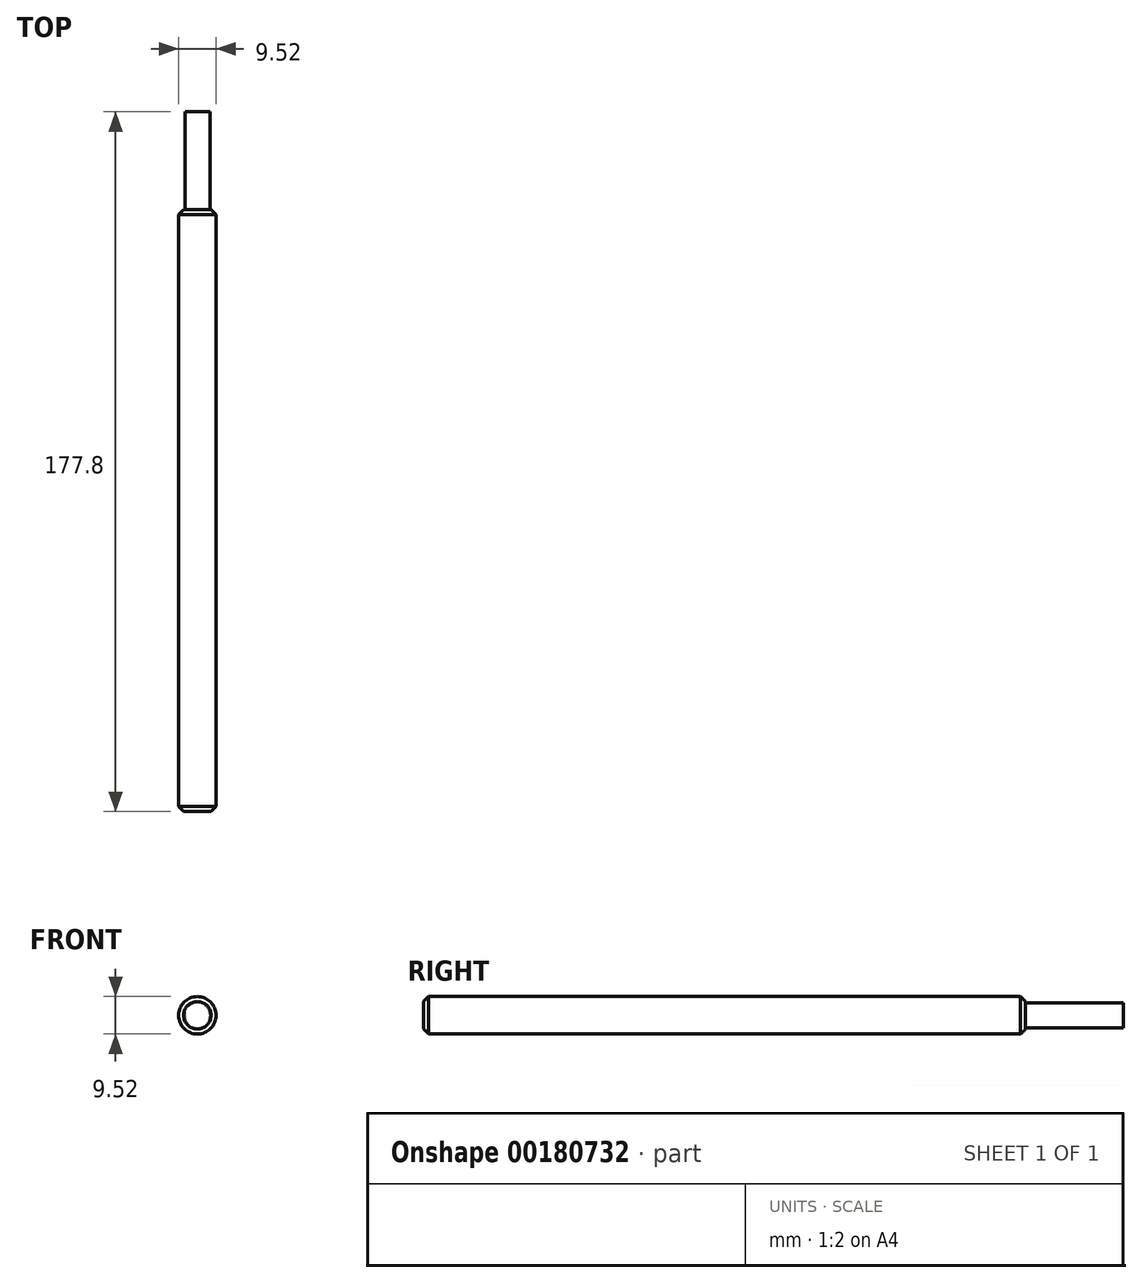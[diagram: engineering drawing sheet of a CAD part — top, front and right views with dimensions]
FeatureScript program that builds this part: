
annotation { "Feature Type Name" : "Feature", "Feature Type Description" : "" }
export const myFeature = defineFeature(function(context is Context, id is Id, definition is map)
    precondition{}
    {
        {
            var Q0;
            Q0=qCreatedBy(makeId("Front.planeOp"),FACE);
            var sketch = newSketch(context, id + "F0", { "sketchPlane" : qUnion([Q0])});
            skCircle(sketch, "E0", {"center": v(0, 0) * mm, "radius": 4.76 * mm});
            skSolve(sketch);
        }
        {
            var Q0;
            Q0=makeQuery(id+"F0.imprint","IMPRINT",FACE,{"disambiguationData":[TD([[makeQuery(id+"F0.imprint","IMPRINT",EDGE,{"derivedFrom":sQuery(id+"F0.wireOp",EDGE,"E0")}),1.0]])]});
            extrude(context, id + "F1", {"entities" : qUnion([Q0]), "depth" : 152.9 * mm});
        }
        {
            var Q0;
            Q0=makeQuery(id+"F1.opExtrude","CAP_EDGE",EDGE,{"disambiguationData":[OSD([sQuery(id+"F0.wireOp",EDGE,"E0")])],"isStart":false});
            var Q1;
            Q1=makeQuery(id+"F1.opExtrude","CAP_EDGE",EDGE,{"disambiguationData":[OSD([sQuery(id+"F0.wireOp",EDGE,"E0")])],"isStart":true});
            chamfer(context, id + "F2", {"entities" : qUnion([Q0, Q1]), "chamferType" : ChamferType.OFFSET_ANGLE, "width" : 1.27 * mm, "oppositeDirection" : false, "angle" : 45 * degree, "tangentPropagation" : true});
        }
        {
            var Q0;
            Q0=makeQuery(id+"F1.opExtrude","CAP_FACE",FACE,{"disambiguationData":[OSD([sQuery(id+"F0.wireOp",EDGE,"E0")])],"isStart":true});
            var sketch = newSketch(context, id + "F3", { "sketchPlane" : qUnion([Q0])});
            skCircle(sketch, "E1", {"center": v(0, 0) * mm, "radius": 3.18 * mm});
            skSolve(sketch);
        }
        {
            var Q0;
            Q0=makeQuery(id+"F3.imprint","IMPRINT",FACE,{"disambiguationData":[TD([[makeQuery(id+"F3.imprint","IMPRINT",EDGE,{"derivedFrom":sQuery(id+"F3.wireOp",EDGE,"E1")}),1.0]])]});
            extrude(context, id + "F4", {"entities" : qUnion([Q0]), "operationType" : NewBodyOperationType.ADD, "depth" : 24.9 * mm});
        }
    });
